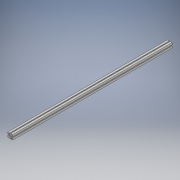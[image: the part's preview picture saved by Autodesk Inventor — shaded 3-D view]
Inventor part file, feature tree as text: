
AUTODESK INVENTOR PART (.ipt)
format: ipt  version: 2018 (Build 220112000, 112)  size: 154,624 bytes
history: native  units: mm
features: extrude x1, sketch x1
ambient origin geometry x8: Origin, YZ Plane, XZ Plane, XY Plane, X Axis, Y Axis, Z Axis, Center Point
bodies: Volumenkörper1 (feature_tree)
feature tree (2):
  extrude  "Extrusion1"  Depth=3.0mm
  sketch  "Skizze1"  dims[d0=3.0mm d1=3.0mm d2=0.5mm d3=1.0mm d4=1.0mm d5=1.2mm d6=1.2mm d7=1.2mm d8=1.2mm d9=0.3mm d10=0.15mm d11=0.15mm d12=0.15mm d13=0.15mm d14=100.0mm d15=0.0mm]
